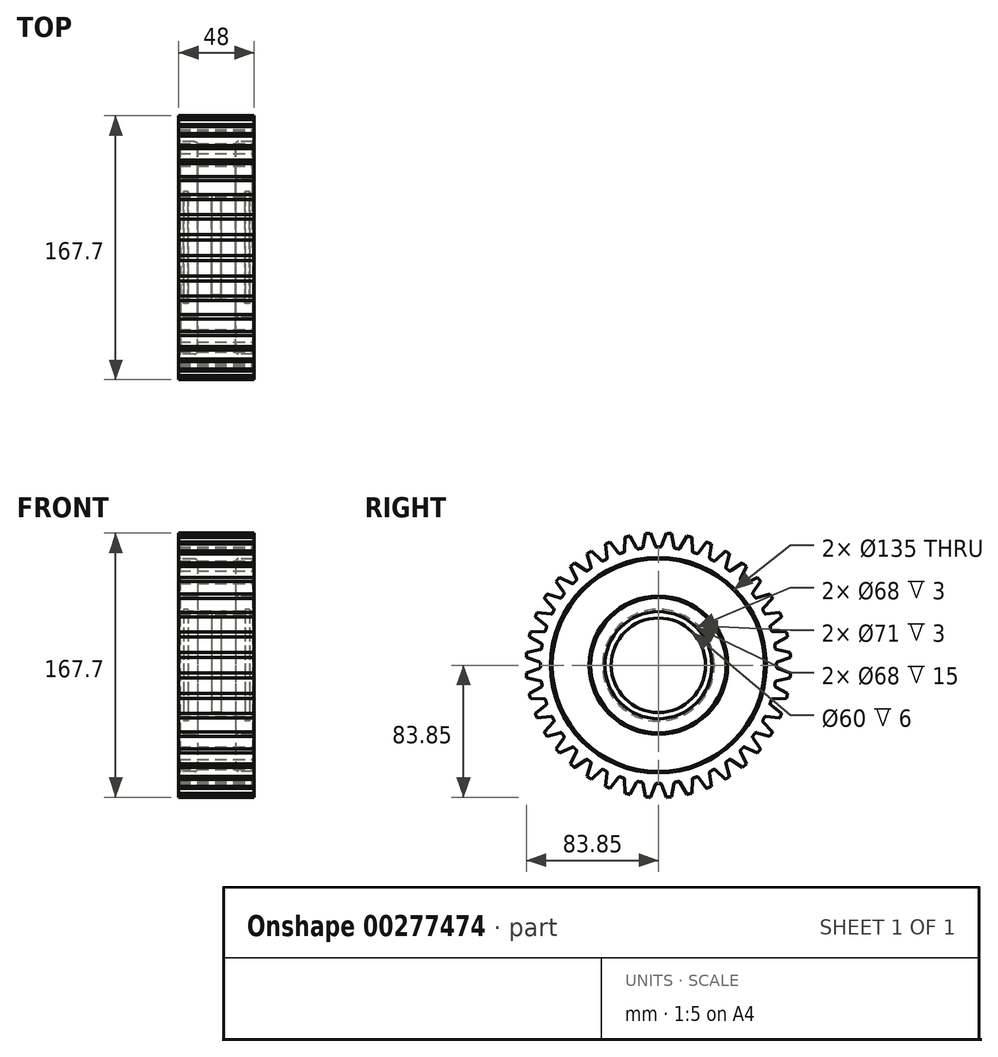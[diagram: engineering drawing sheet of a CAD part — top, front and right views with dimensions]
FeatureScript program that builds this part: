
annotation { "Feature Type Name" : "Feature", "Feature Type Description" : "" }
export const myFeature = defineFeature(function(context is Context, id is Id, definition is map)
    precondition{}
    {
        {
            var Q0;
            Q0=qCreatedBy(makeId("Front.planeOp"),FACE);
            var sketch = newSketch(context, id + "F0", { "sketchPlane" : qUnion([Q0])});
            skLineSegment(sketch, "E0.bottom", {"start": v(-24, 84) * mm, "end": v(0, 84) * mm});
            skLineSegment(sketch, "E0.left", {"start": v(-24, 84) * mm, "end": v(-24, 67.5) * mm});
            skLineSegment(sketch, "E0.right", {"start": v(0, 84) * mm, "end": v(0, 0) * mm, "construction": true});
            skLineSegment(sketch, "E1", {"start": v(-24, 34) * mm, "end": v(-21, 34) * mm});
            skLineSegment(sketch, "E2", {"start": v(-21, 34) * mm, "end": v(-21, 35.5) * mm});
            skLineSegment(sketch, "E3", {"start": v(-21, 35.5) * mm, "end": v(-18, 35.5) * mm});
            skLineSegment(sketch, "E4", {"start": v(-18, 35.5) * mm, "end": v(-18, 34) * mm});
            skLineSegment(sketch, "E5", {"start": v(-18, 34) * mm, "end": v(-3, 34) * mm});
            skLineSegment(sketch, "E6", {"start": v(-3, 34) * mm, "end": v(-3, 30) * mm});
            skLineSegment(sketch, "E7", {"start": v(-3, 30) * mm, "end": v(0, 30) * mm});
            skLineSegment(sketch, "E8", {"start": v(-24, 0) * mm, "end": v(0, 0) * mm, "construction": true});
            skLineSegment(sketch, "E9", {"start": v(-24, 44) * mm, "end": v(-14, 44) * mm});
            skLineSegment(sketch, "E10", {"start": v(-12, 46) * mm, "end": v(-12, 65.5) * mm});
            skLineSegment(sketch, "E11", {"start": v(-14, 67.5) * mm, "end": v(-24, 67.5) * mm});
            skLineSegment(sketch, "E12.trimOffspring", {"start": v(-24, 44) * mm, "end": v(-24, 34) * mm});
            skPoint(sketch, "E13.visualSharp", {"position": v(-12, 67.5) * mm});
            skArc(sketch, "E13.filletArc", {"start": v(-12, 65.5) * mm, "mid": v(-12.59, 66.91) * mm, "end": v(-14, 67.5) * mm});
            skPoint(sketch, "E14.visualSharp", {"position": v(-12, 44) * mm});
            skArc(sketch, "E14.filletArc", {"start": v(-14, 44) * mm, "mid": v(-12.59, 44.59) * mm, "end": v(-12, 46) * mm});
            skArc(sketch, "E15.MirrorCS", {"start": v(12, 65.5) * mm, "mid": v(12.59, 66.91) * mm, "end": v(14, 67.5) * mm});
            skArc(sketch, "E16.MirrorCS", {"start": v(14, 44) * mm, "mid": v(12.59, 44.59) * mm, "end": v(12, 46) * mm});
            skLineSegment(sketch, "E17.MirrorCS", {"start": v(21, 35.5) * mm, "end": v(18, 35.5) * mm});
            skLineSegment(sketch, "E18.MirrorCS", {"start": v(21, 34) * mm, "end": v(21, 35.5) * mm});
            skLineSegment(sketch, "E19.MirrorCS", {"start": v(24, 34) * mm, "end": v(21, 34) * mm});
            skLineSegment(sketch, "E20.MirrorCS", {"start": v(18, 35.5) * mm, "end": v(18, 34) * mm});
            skLineSegment(sketch, "E21.MirrorCS", {"start": v(3, 34) * mm, "end": v(3, 30) * mm});
            skLineSegment(sketch, "E22.MirrorCS", {"start": v(3, 30) * mm, "end": v(0, 30) * mm});
            skLineSegment(sketch, "E23.MirrorCS", {"start": v(24, 44) * mm, "end": v(24, 34) * mm});
            skLineSegment(sketch, "E24.MirrorCS", {"start": v(14, 67.5) * mm, "end": v(24, 67.5) * mm});
            skLineSegment(sketch, "E25.MirrorCS", {"start": v(24, 84) * mm, "end": v(0, 84) * mm});
            skLineSegment(sketch, "E26.MirrorCS", {"start": v(12, 46) * mm, "end": v(12, 65.5) * mm});
            skPoint(sketch, "E27.MirrorP", {"position": v(12, 44) * mm});
            skLineSegment(sketch, "E28.MirrorCS", {"start": v(24, 44) * mm, "end": v(14, 44) * mm});
            skLineSegment(sketch, "E29.MirrorCS", {"start": v(24, 0) * mm, "end": v(0, 0) * mm, "construction": true});
            skLineSegment(sketch, "E30.MirrorCS", {"start": v(24, 84) * mm, "end": v(24, 67.5) * mm});
            skLineSegment(sketch, "E31.MirrorCS", {"start": v(18, 34) * mm, "end": v(3, 34) * mm});
            skPoint(sketch, "E32.MirrorP", {"position": v(12, 67.5) * mm});
            skSolve(sketch);
        }
        {
            var Q0;
            Q0=makeQuery(id+"F0.imprint","IMPRINT",FACE,{"disambiguationData":[TD([[makeQuery(id+"F0.imprint","IMPRINT",EDGE,{"derivedFrom":sQuery(id+"F0.wireOp",EDGE,"E0.bottom")}),-1.0]])]});
            var Q1;
            Q1=sQuery(id+"F0.wireOp",EDGE,"E8");
            revolve(context, id + "F1", {"entities" : qUnion([Q0]), "axis" : qUnion([Q1]), "revolveType" : RevolveType.FULL});
        }
        {
            var Q0;
            Q0=qCreatedBy(makeId("Right.planeOp"),FACE);
            var sketch = newSketch(context, id + "F2", { "sketchPlane" : qUnion([Q0])});
            skArc(sketch, "E33", {"start": v(1.04, 75) * mm, "mid": v(0, 75) * mm, "end": v(-1.04, 75) * mm});
            skLineSegment(sketch, "E34", {"start": v(0, 0) * mm, "end": v(0, 84) * mm, "construction": true});
            skLineSegment(sketch, "E35", {"start": v(2, 75.65) * mm, "end": v(4.98, 83.85) * mm});
            skLineSegment(sketch, "E36.MirrorCS", {"start": v(-2, 75.65) * mm, "end": v(-4.98, 83.85) * mm});
            skPoint(sketch, "E37.visualSharp", {"position": v(-1.75, 74.98) * mm});
            skArc(sketch, "E37.filletArc", {"start": v(-2, 75.65) * mm, "mid": v(-1.62, 75.17) * mm, "end": v(-1.04, 75) * mm});
            skPoint(sketch, "E38.visualSharp", {"position": v(1.75, 74.98) * mm});
            skArc(sketch, "E38.filletArc", {"start": v(1.04, 75) * mm, "mid": v(1.62, 75.17) * mm, "end": v(2, 75.65) * mm});
            skLineSegment(sketch, "E39", {"start": v(-4.98, 83.85) * mm, "end": v(4.98, 83.85) * mm});
            skLineSegment(sketch, "E40", {"start": v(-4.98, 83.85) * mm, "end": v(-7.32, 90.3) * mm});
            skLineSegment(sketch, "E41", {"start": v(4.98, 83.85) * mm, "end": v(7.32, 90.3) * mm});
            skLineSegment(sketch, "E42", {"start": v(-7.32, 90.3) * mm, "end": v(7.32, 90.3) * mm});
            skSolve(sketch);
        }
        {
            var Q0;
            Q0 = qSketchRegion(id + "F2", true);
            extrude(context, id + "F3", {"entities" : qUnion([Q0]), "operationType" : NewBodyOperationType.REMOVE, "endBound" : BoundingType.SYMMETRIC, "oppositeDirection" : true, "depth" : 50 * mm});
        }
        {
            var Q0;
            Q0=makeQuery(id+"F3.boolean.opBoolean","COPY",FACE,{"derivedFrom":makeQuery(id+"F3.opExtrude","SWEPT_FACE",FACE,{"disambiguationData":[OSD([sQuery(id+"F2.wireOp",EDGE,"E36.MirrorCS"),sQuery(id+"F2.wireOp",EDGE,"E40")])]})});
            var Q1;
            Q1=makeQuery(id+"F3.boolean.opBoolean","COPY",FACE,{"derivedFrom":makeQuery(id+"F3.opExtrude","SWEPT_FACE",FACE,{"disambiguationData":[OSD([sQuery(id+"F2.wireOp",EDGE,"E37.filletArc")])]})});
            var Q2;
            Q2=makeQuery(id+"F3.boolean.opBoolean","COPY",FACE,{"derivedFrom":makeQuery(id+"F3.opExtrude","SWEPT_FACE",FACE,{"disambiguationData":[OSD([sQuery(id+"F2.wireOp",EDGE,"E33")])]})});
            var Q3;
            Q3=makeQuery(id+"F3.boolean.opBoolean","COPY",FACE,{"derivedFrom":makeQuery(id+"F3.opExtrude","SWEPT_FACE",FACE,{"disambiguationData":[OSD([sQuery(id+"F2.wireOp",EDGE,"E38.filletArc")])]})});
            var Q4;
            Q4=makeQuery(id+"F3.boolean.opBoolean","COPY",FACE,{"derivedFrom":makeQuery(id+"F3.opExtrude","SWEPT_FACE",FACE,{"disambiguationData":[OSD([sQuery(id+"F2.wireOp",EDGE,"E35"),sQuery(id+"F2.wireOp",EDGE,"E41")])]})});
            var Q5;
            Q5=makeQuery(id+"F1.opRevolve","SWEPT_FACE",FACE,{"disambiguationData":[OSD([sQuery(id+"F0.wireOp",EDGE,"E0.bottom"),sQuery(id+"F0.wireOp",EDGE,"E25.MirrorCS")])]});
            circularPattern(context, id + "F4", {"patternType" : PatternType.FACE, "faces" : qUnion([Q0, Q1, Q2, Q3, Q4]), "axis" : qUnion([Q5]), "angle" : 9 * degree, "instanceCount" : 40, "oppositeDirection" : true});
        }
        {
            var Q0;
            Q0=makeQuery(id+"F1.opRevolve","SWEPT_EDGE",EDGE,{"disambiguationData":[OSD([sQuery(id+"F0.wireOp",EDGE,"E24.MirrorCS"),sQuery(id+"F0.wireOp",EDGE,"E30.MirrorCS")])]});
            var Q1;
            Q1=makeQuery(id+"F1.opRevolve","SWEPT_EDGE",EDGE,{"disambiguationData":[OSD([sQuery(id+"F0.wireOp",EDGE,"E0.left"),sQuery(id+"F0.wireOp",EDGE,"E11")])]});
            var Q2;
            Q2=makeQuery(id+"F1.opRevolve","SWEPT_EDGE",EDGE,{"disambiguationData":[OSD([sQuery(id+"F0.wireOp",EDGE,"E9"),sQuery(id+"F0.wireOp",EDGE,"E12.trimOffspring")])]});
            var Q3;
            Q3=makeQuery(id+"F1.opRevolve","SWEPT_EDGE",EDGE,{"disambiguationData":[OSD([sQuery(id+"F0.wireOp",EDGE,"E23.MirrorCS"),sQuery(id+"F0.wireOp",EDGE,"E28.MirrorCS")])]});
            chamfer(context, id + "F5", {"entities" : qUnion([Q0, Q1, Q2, Q3]), "chamferType" : ChamferType.OFFSET_ANGLE, "width" : 1 * mm, "oppositeDirection" : false, "angle" : 45 * degree, "tangentPropagation" : true});
        }
    });
